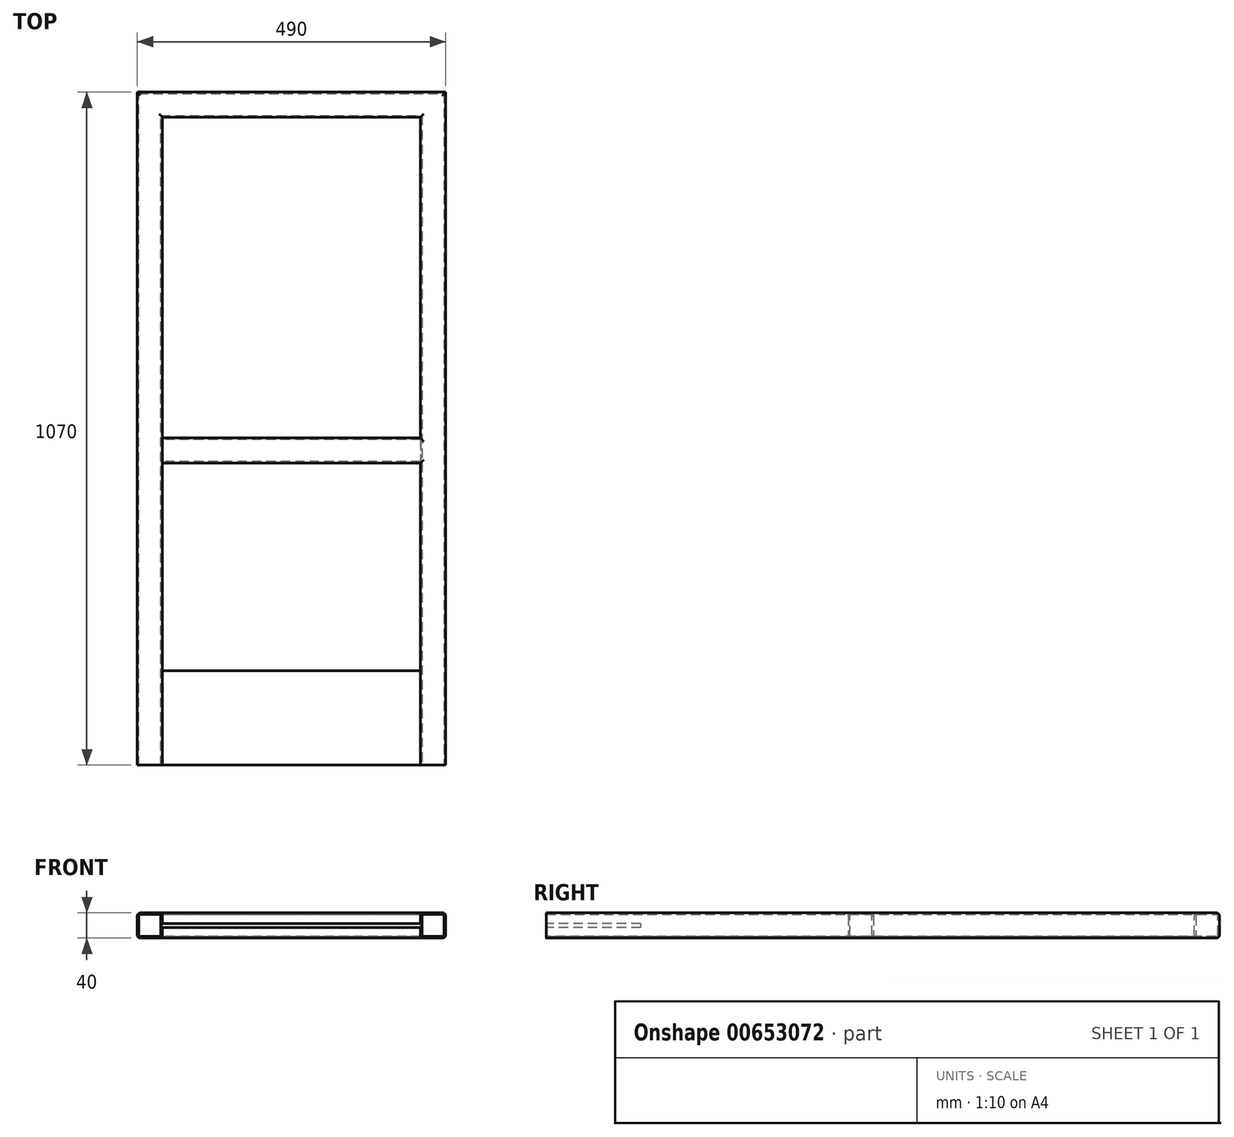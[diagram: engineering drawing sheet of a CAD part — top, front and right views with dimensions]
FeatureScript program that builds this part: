
annotation { "Feature Type Name" : "Feature", "Feature Type Description" : "" }
export const myFeature = defineFeature(function(context is Context, id is Id, definition is map)
    precondition{}
    {
        {
            var Q0;
            Q0=qCreatedBy(makeId("Front.planeOp"),FACE);
            var sketch = newSketch(context, id + "F0", { "sketchPlane" : qUnion([Q0])});
            skLineSegment(sketch, "E0.bottom", {"start": v(15, -20) * mm, "end": v(-15, -20) * mm});
            skLineSegment(sketch, "E0.top", {"start": v(15, 20) * mm, "end": v(-15, 20) * mm});
            skLineSegment(sketch, "E0.left", {"start": v(20, -15) * mm, "end": v(20, 15) * mm});
            skLineSegment(sketch, "E0.right", {"start": v(-20, -15) * mm, "end": v(-20, 15) * mm});
            skPoint(sketch, "E0.middle", {"position": v(0, 0) * mm});
            skPoint(sketch, "E1.visualSharp", {"position": v(-20, 20) * mm});
            skArc(sketch, "E1.filletArc", {"start": v(-15, 20) * mm, "mid": v(-18.54, 18.54) * mm, "end": v(-20, 15) * mm});
            skPoint(sketch, "E2.visualSharp", {"position": v(20, 20) * mm});
            skArc(sketch, "E2.filletArc", {"start": v(20, 15) * mm, "mid": v(18.54, 18.54) * mm, "end": v(15, 20) * mm});
            skPoint(sketch, "E3.visualSharp", {"position": v(20, -20) * mm});
            skArc(sketch, "E3.filletArc", {"start": v(15, -20) * mm, "mid": v(18.54, -18.54) * mm, "end": v(20, -15) * mm});
            skPoint(sketch, "E4.visualSharp", {"position": v(-20, -20) * mm});
            skArc(sketch, "E4.filletArc", {"start": v(-20, -15) * mm, "mid": v(-18.54, -18.54) * mm, "end": v(-15, -20) * mm});
            skArc(sketch, "E5.0", {"start": v(-17.5, -15) * mm, "mid": v(-16.77, -16.77) * mm, "end": v(-15, -17.5) * mm});
            skLineSegment(sketch, "E5.1", {"start": v(15, -17.5) * mm, "end": v(-15, -17.5) * mm});
            skLineSegment(sketch, "E5.2", {"start": v(-17.5, -15) * mm, "end": v(-17.5, 15) * mm});
            skArc(sketch, "E5.3", {"start": v(15, -17.5) * mm, "mid": v(16.77, -16.77) * mm, "end": v(17.5, -15) * mm});
            skArc(sketch, "E5.4", {"start": v(-15, 17.5) * mm, "mid": v(-16.77, 16.77) * mm, "end": v(-17.5, 15) * mm});
            skLineSegment(sketch, "E5.5", {"start": v(15, 17.5) * mm, "end": v(-15, 17.5) * mm});
            skArc(sketch, "E5.6", {"start": v(17.5, 15) * mm, "mid": v(16.77, 16.77) * mm, "end": v(15, 17.5) * mm});
            skLineSegment(sketch, "E5.7", {"start": v(17.5, -15) * mm, "end": v(17.5, 15) * mm});
            skSolve(sketch);
        }
        {
            var Q0;
            Q0=qCreatedBy(makeId("Top.planeOp"),FACE);
            var sketch = newSketch(context, id + "F1", { "sketchPlane" : qUnion([Q0])});
            skLineSegment(sketch, "E6.bottom", {"start": v(0, 0) * mm, "end": v(450, 0) * mm});
            skLineSegment(sketch, "E6.top", {"start": v(0, 1050) * mm, "end": v(450, 1050) * mm});
            skLineSegment(sketch, "E6.left", {"start": v(0, 0) * mm, "end": v(0, 1050) * mm});
            skLineSegment(sketch, "E6.right", {"start": v(450, 0) * mm, "end": v(450, 1050) * mm});
            skSolve(sketch);
        }
        {
            var Q0;
            Q0=makeQuery(id+"F0.imprint","IMPRINT",FACE,{"disambiguationData":[TD([[makeQuery(id+"F0.imprint","IMPRINT",EDGE,{"derivedFrom":sQuery(id+"F0.wireOp",EDGE,"E0.bottom")}),-1.0]])]});
            var Q1;
            Q1=sQuery(id+"F1.wireOp",EDGE,"E6.left");
            var Q2;
            Q2=sQuery(id+"F1.wireOp",EDGE,"E6.top");
            var Q3;
            Q3=sQuery(id+"F1.wireOp",EDGE,"E6.right");
            sweep(context, id + "F2", {"profiles" : qUnion([Q0]), "path" : qUnion([Q1, Q2, Q3])});
        }
        {
            var Q0;
            Q0=makeQuery(id+"F2.opSweep","SWEPT_FACE",FACE,{"disambiguationData":[OSD([sQuery(id+"F0.wireOp",EDGE,"E0.left"),sQuery(id+"F1.wireOp",EDGE,"E6.left")])]});
            var sketch = newSketch(context, id + "F3", { "sketchPlane" : qUnion([Q0])});
            skLineSegment(sketch, "E7.bottom", {"start": v(515, -20) * mm, "end": v(485, -20) * mm});
            skLineSegment(sketch, "E7.top", {"start": v(515, 20) * mm, "end": v(485, 20) * mm});
            skLineSegment(sketch, "E7.left", {"start": v(520, -15) * mm, "end": v(520, 15) * mm});
            skLineSegment(sketch, "E7.right", {"start": v(480, -15) * mm, "end": v(480, 15) * mm});
            skPoint(sketch, "E7.middle", {"position": v(500, 0) * mm});
            skPoint(sketch, "E8.visualSharp", {"position": v(480, 20) * mm});
            skArc(sketch, "E8.filletArc", {"start": v(485, 20) * mm, "mid": v(481.46, 18.54) * mm, "end": v(480, 15) * mm});
            skPoint(sketch, "E9.visualSharp", {"position": v(520, 20) * mm});
            skArc(sketch, "E9.filletArc", {"start": v(520, 15) * mm, "mid": v(518.54, 18.54) * mm, "end": v(515, 20) * mm});
            skPoint(sketch, "E10.visualSharp", {"position": v(520, -20) * mm});
            skArc(sketch, "E10.filletArc", {"start": v(515, -20) * mm, "mid": v(518.54, -18.54) * mm, "end": v(520, -15) * mm});
            skPoint(sketch, "E11.visualSharp", {"position": v(480, -20) * mm});
            skArc(sketch, "E11.filletArc", {"start": v(480, -15) * mm, "mid": v(481.46, -18.54) * mm, "end": v(485, -20) * mm});
            skArc(sketch, "E12.0", {"start": v(482.5, -15) * mm, "mid": v(483.23, -16.77) * mm, "end": v(485, -17.5) * mm});
            skLineSegment(sketch, "E12.1", {"start": v(515, -17.5) * mm, "end": v(485, -17.5) * mm});
            skLineSegment(sketch, "E12.2", {"start": v(482.5, -15) * mm, "end": v(482.5, 15) * mm});
            skArc(sketch, "E12.3", {"start": v(515, -17.5) * mm, "mid": v(516.77, -16.77) * mm, "end": v(517.5, -15) * mm});
            skArc(sketch, "E12.4", {"start": v(485, 17.5) * mm, "mid": v(483.23, 16.77) * mm, "end": v(482.5, 15) * mm});
            skLineSegment(sketch, "E12.5", {"start": v(515, 17.5) * mm, "end": v(485, 17.5) * mm});
            skArc(sketch, "E12.6", {"start": v(517.5, 15) * mm, "mid": v(516.77, 16.77) * mm, "end": v(515, 17.5) * mm});
            skLineSegment(sketch, "E12.7", {"start": v(517.5, -15) * mm, "end": v(517.5, 15) * mm});
            skLineSegment(sketch, "E13.0", {"start": v(0, 20) * mm, "end": v(1035, 20) * mm, "construction": true});
            skSolve(sketch);
        }
        {
            var Q0;
            Q0 = qSketchRegion(id + "F3", true);
            extrude(context, id + "F4", {"entities" : qUnion([Q0]), "operationType" : NewBodyOperationType.ADD, "endBound" : BoundingType.UP_TO_NEXT, "depth" : 25 * mm, "offsetDistance" : 25 * mm});
        }
        {
            var Q0;
            {var subQ2=sQuery(id+"F3.wireOp",EDGE,"E7.right");var subQ3=sQuery(id+"F1.wireOp",EDGE,"E6.left");var subQ6=sQuery(id+"F0.wireOp",EDGE,"E0.left");Q0=makeQuery(id+"F4.boolean.opBoolean","SPLIT",FACE,{"disambiguationData":[TD([makeQuery(id+"F4.opExtrude","SWEPT_FACE",FACE,{"disambiguationData":[OSD([subQ2])]})])],"derivedFrom":makeQuery(id+"F2.opSweep","SWEPT_FACE",FACE,{"disambiguationData":[OSD([subQ6,subQ3])]})});}
            var sketch = newSketch(context, id + "F5", { "sketchPlane" : qUnion([Q0])});
            skLineSegment(sketch, "E14.bottom", {"start": v(0, -3) * mm, "end": v(150, -3) * mm});
            skLineSegment(sketch, "E14.top", {"start": v(0, 3) * mm, "end": v(150, 3) * mm});
            skLineSegment(sketch, "E14.left", {"start": v(0, -3) * mm, "end": v(0, 3) * mm});
            skLineSegment(sketch, "E14.right", {"start": v(150, -3) * mm, "end": v(150, 3) * mm});
            skSolve(sketch);
        }
        {
            var Q0;
            Q0 = qSketchRegion(id + "F5", true);
            extrude(context, id + "F6", {"entities" : qUnion([Q0]), "operationType" : NewBodyOperationType.ADD, "endBound" : BoundingType.UP_TO_NEXT, "depth" : 25 * mm, "offsetDistance" : 25 * mm});
        }
    });
